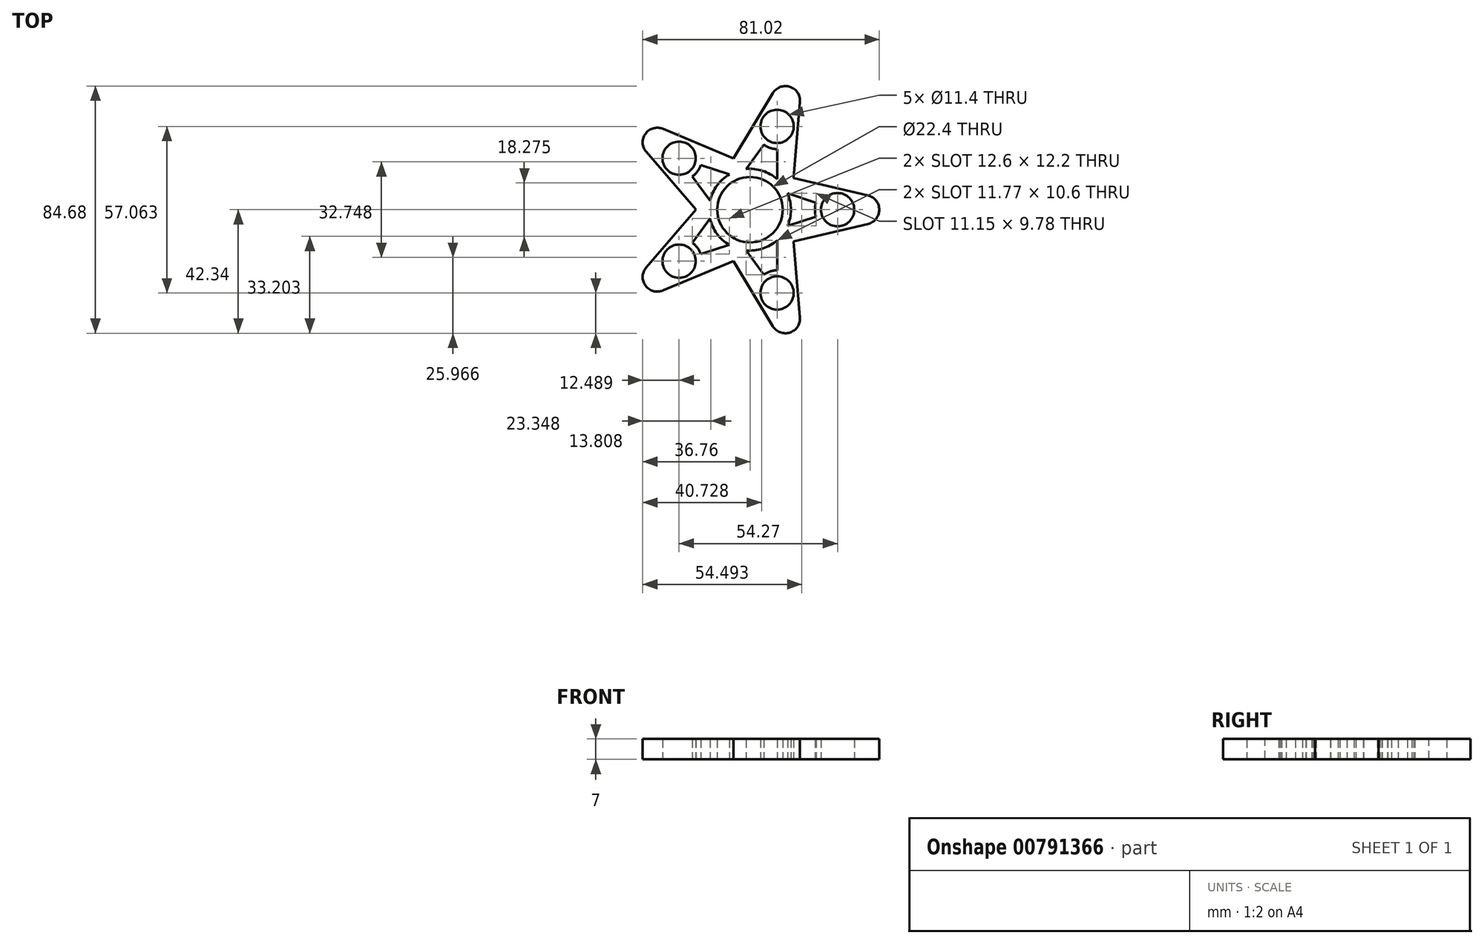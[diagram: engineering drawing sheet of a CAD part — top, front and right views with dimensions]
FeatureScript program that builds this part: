
annotation { "Feature Type Name" : "Feature", "Feature Type Description" : "" }
export const myFeature = defineFeature(function(context is Context, id is Id, definition is map)
    precondition{}
    {
        {
            var Q0;
            Q0=qCreatedBy(makeId("Top.planeOp"),FACE);
            var sketch = newSketch(context, id + "F0", { "sketchPlane" : qUnion([Q0])});
            skCircle(sketch, "E0", {"center": v(0, 0) * mm, "radius": 11.2 * mm});
            skArc(sketch, "E1", {"start": v(9.27, 10.5) * mm, "mid": v(4.33, 13.31) * mm, "end": v(-1.33, 13.94) * mm});
            skCircle(sketch, "E2", {"center": v(30, 0) * mm, "radius": 5.7 * mm});
            skLineSegment(sketch, "E3", {"start": v(61.07, 0) * mm, "end": v(14.95, 10.86) * mm});
            skLineSegment(sketch, "E4", {"start": v(61.07, 0) * mm, "end": v(14.95, -10.86) * mm});
            skLineSegment(sketch, "E5.1.0", {"start": v(18.87, 58.08) * mm, "end": v(-5.71, 17.58) * mm});
            skCircle(sketch, "E5.1.1", {"center": v(9.27, 28.53) * mm, "radius": 5.7 * mm});
            skLineSegment(sketch, "E5.1.2", {"start": v(18.87, 58.08) * mm, "end": v(14.95, 10.86) * mm});
            skLineSegment(sketch, "E5.2.0", {"start": v(-49.4, 35.9) * mm, "end": v(-18.48, 0) * mm});
            skCircle(sketch, "E5.2.1", {"center": v(-24.27, 17.63) * mm, "radius": 5.7 * mm});
            skLineSegment(sketch, "E5.2.2", {"start": v(-49.4, 35.9) * mm, "end": v(-5.71, 17.58) * mm});
            skLineSegment(sketch, "E6.2.3.0", {"start": v(-49.4, -35.9) * mm, "end": v(-5.71, -17.58) * mm});
            skCircle(sketch, "E6.3.3.0", {"center": v(-24.27, -17.63) * mm, "radius": 5.7 * mm});
            skLineSegment(sketch, "E6.5.3.0", {"start": v(-49.4, -35.9) * mm, "end": v(-18.48, 0) * mm});
            skLineSegment(sketch, "E7.2.4.0", {"start": v(18.87, -58.08) * mm, "end": v(14.95, -10.86) * mm});
            skCircle(sketch, "E7.3.4.0", {"center": v(9.27, -28.53) * mm, "radius": 5.7 * mm});
            skLineSegment(sketch, "E7.5.4.0", {"start": v(18.87, -58.08) * mm, "end": v(-5.71, -17.58) * mm});
            skLineSegment(sketch, "E8", {"start": v(4.71, 22.26) * mm, "end": v(-1.33, 13.94) * mm});
            skLineSegment(sketch, "E9", {"start": v(9.27, 20.78) * mm, "end": v(9.27, 10.5) * mm});
            skLineSegment(sketch, "E10", {"start": v(22.62, -2.4) * mm, "end": v(12.84, -5.57) * mm});
            skArc(sketch, "E11", {"start": v(4.71, 22.26) * mm, "mid": v(6.87, 21.15) * mm, "end": v(9.27, 20.78) * mm});
            skArc(sketch, "E12.1.0", {"start": v(-19.71, 11.36) * mm, "mid": v(-18, 13.07) * mm, "end": v(-16.9, 15.24) * mm});
            skArc(sketch, "E12.2.0", {"start": v(-16.9, -15.24) * mm, "mid": v(-18, -13.07) * mm, "end": v(-19.71, -11.36) * mm});
            skArc(sketch, "E12.3.0", {"start": v(9.27, -20.78) * mm, "mid": v(6.87, -21.15) * mm, "end": v(4.71, -22.26) * mm});
            skArc(sketch, "E12.4.0", {"start": v(22.62, 2.4) * mm, "mid": v(22.24, 0) * mm, "end": v(22.62, -2.4) * mm});
            skLineSegment(sketch, "E13.trimOffspring", {"start": v(12.84, 5.57) * mm, "end": v(22.62, 2.4) * mm});
            skLineSegment(sketch, "E14.trimOffspring", {"start": v(4.71, -22.26) * mm, "end": v(-1.33, -13.94) * mm});
            skLineSegment(sketch, "E15.trimOffspring", {"start": v(9.27, -10.5) * mm, "end": v(9.27, -20.78) * mm});
            skLineSegment(sketch, "E16.trimOffspring", {"start": v(-7.11, -12.06) * mm, "end": v(-16.9, -15.24) * mm});
            skLineSegment(sketch, "E17.trimOffspring", {"start": v(-16.9, 15.24) * mm, "end": v(-7.11, 12.06) * mm});
            skLineSegment(sketch, "E18.trimOffspring", {"start": v(-13.67, 3.04) * mm, "end": v(-19.71, 11.36) * mm});
            skLineSegment(sketch, "E19.trimOffspring", {"start": v(-13.67, -3.04) * mm, "end": v(-19.71, -11.36) * mm});
            skArc(sketch, "E20.trimOffspring", {"start": v(12.84, -5.57) * mm, "mid": v(14, 0) * mm, "end": v(12.84, 5.57) * mm});
            skArc(sketch, "E21.trimOffspring", {"start": v(-1.33, -13.94) * mm, "mid": v(4.33, -13.31) * mm, "end": v(9.27, -10.5) * mm});
            skArc(sketch, "E22.trimOffspring", {"start": v(-13.67, -3.04) * mm, "mid": v(-11.33, -8.23) * mm, "end": v(-7.11, -12.06) * mm});
            skArc(sketch, "E23.trimOffspring", {"start": v(-7.11, 12.06) * mm, "mid": v(-11.33, 8.23) * mm, "end": v(-13.67, 3.04) * mm});
            skSolve(sketch);
        }
        {
            var Q0;
            Q0=makeQuery(id+"F0.imprint","IMPRINT",FACE,{"disambiguationData":[TD([[makeQuery(id+"F0.imprint","IMPRINT",EDGE,{"derivedFrom":sQuery(id+"F0.wireOp",EDGE,"E0")}),-1.0]])]});
            extrude(context, id + "F1", {"entities" : qUnion([Q0]), "depth" : 7 * mm, "offsetDistance" : 25 * mm});
        }
        {
            var Q0;
            Q0=makeQuery(id+"F1.opExtrude","SWEPT_EDGE",EDGE,{"disambiguationData":[OSD([sQuery(id+"F0.wireOp",EDGE,"E7.2.4.0"),sQuery(id+"F0.wireOp",EDGE,"E7.5.4.0")])]});
            var Q1;
            Q1=makeQuery(id+"F1.opExtrude","SWEPT_EDGE",EDGE,{"disambiguationData":[OSD([sQuery(id+"F0.wireOp",EDGE,"E3"),sQuery(id+"F0.wireOp",EDGE,"E4")])]});
            var Q2;
            Q2=makeQuery(id+"F1.opExtrude","SWEPT_EDGE",EDGE,{"disambiguationData":[OSD([sQuery(id+"F0.wireOp",EDGE,"E5.1.0"),sQuery(id+"F0.wireOp",EDGE,"E5.1.2")])]});
            var Q3;
            Q3=makeQuery(id+"F1.opExtrude","SWEPT_EDGE",EDGE,{"disambiguationData":[OSD([sQuery(id+"F0.wireOp",EDGE,"E5.2.0"),sQuery(id+"F0.wireOp",EDGE,"E5.2.2")])]});
            var Q4;
            Q4=makeQuery(id+"F1.opExtrude","SWEPT_EDGE",EDGE,{"disambiguationData":[OSD([sQuery(id+"F0.wireOp",EDGE,"E6.2.3.0"),sQuery(id+"F0.wireOp",EDGE,"E6.5.3.0")])]});
            fillet(context, id + "F2", {"entities" : qUnion([Q0, Q1, Q2, Q3, Q4]), "radius" : 5 * mm, "tangentPropagation" : true, "allowEdgeOverflow" : false});
        }
    });
